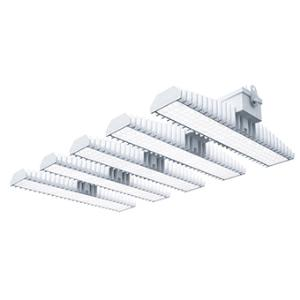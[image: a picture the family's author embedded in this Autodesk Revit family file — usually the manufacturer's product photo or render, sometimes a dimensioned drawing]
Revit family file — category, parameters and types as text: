
# Revit family: 3f_filippi_-_3f_lem_ho_ampio_3f_filippi_-_58958_a0812_-_3f_lem_5_ho_led_350_cr_ampio___vs_2ddf
name_source: partatom
category: Lighting Fixtures
units: mm (PartAtom-declared; Revit-internal decimal feet)

## family parameters
Cut with Voids When Loaded = No
Host = Face
Light Source = No
Part Type = Normal
Room Calculation Point = No
Round Connector Dimension = Use Diameter
Shared = No

## types (1)
- 3F Filippi - 3F LEM HO Ampio (1 x LED, 44256 lm, 345 W, 4000 K)
    Apparent Load = 345 VA
    Approval mark = CE
    CIE Flux Codes = 67 90 97 100 100
    Color Rendering = 80
    Color Temperature = 4000 K
    Control Gear = Electronic ballast
    Default Elevation = 1800 mm
    Description = Industrial luminaire with high light output and high luminous efficiency designed with the most innovative technologies for environments with temperature up to 55°C.

ILLUMINOTECHNICAL
Luminous efficiency 100% (DLOR 98%, ULOR 2%).
Initial luminous flux of the luminaire 44256 lm.
Direct symmetric wide distribution: the illuminated area has a rectangular shape.
Installation Interdistance Transv.D = 1.24 x hu - Long.D = 1.20 x hu.
Tabular UGR (CIE 117 - 4H-8H; S=0.25H; 70/50/20): RUG 23.8 - 23.9.
Beam angle: 82° - 83°.
Luminous efficacy 128 lm/W.
Lifetime (L93/B10): 30000 h. (tq+25°C)
Lifetime (L90/B10): 50000 h. (tq+25°C)
Lifetime (L85/B10): 80000 h. (tq+25°C)
Lifetime (L80/B10): 100000 h. (tq+25°C)
Lifetime (L85/B10): 50000 h. (tq+55°C)
Sudden decreased luminous flux after 50000 hours: 0% (C0).
Photobiological safety in compliance with IEC/TR 62778: RG0 risk exempt, (IEC 62471).
In compliance with IEC/EN 62722-2-1 - IEC/EN 62717 standards.

SOURCE
5 Mid-Power linear LED modules 70W/840.
Energy efficiency class (UE 2019/2020 - UE 2019/2015): C.
CIE 13.3 Colour rendering index: CRI >80 (R9 <50%).
IES TM-30 Fidelity Index: Rf = 84 Rg = 95.
CCT nominal colour temperature 4000 K.
Colour initial tolerance (MacAdam): SDCM 3.

MECHANICAL
Passive modular heatsinks in die-casted aluminium, painted in white colour.
To optimize the thermal management of the LED module, the heatsinks are oversized and provided with self-cleaning of cooling fins.
Wiring body in aluminium and galvanised steel anchored solidly to the sinks and thermally separated.
3F Lens lenses with high luminous efficiency, transparent methacrylate (PMMA), fixed to the LED modules.
Fixing brackets in stainless steel.
Luminaire with limited surface temperature. - D - (EN 60598-2-24)
Dimensions: 952x542 mm, height 133 mm. Weight 24.37 kg.
IP65 protection degree.
Mechanical strength to impacts IK06 (1 joule).
Glow-wire test resistance 650°C.

ELECTRICAL
Halogen Free electronic wiring 230V-50/60Hz, power factor 0.97, THD <25%, constant output current, class I, 3 driver.
Power of the luminaire 345 W.
ENEC - CE.
SAFE FLICKER: PstLM=<1 and SVM=<0.4 (IEC TR 61547-1 and IEC TR 63158), to ensure a more comfortable and safe light.
Luminaire compliant with EN 60598-2-22 for power supply from a centralised emergency system CPSS (Central Power Supply System), not incorporated in the luminaire - high risk areas excluded. The default power and flux are 100% in AC and 100% in DC.
Ambient temperature from -30°C to +55°C.
Temperature class T6 max 85°C.
Quick connection via M20 3P connector with 9-13 mm tightening range.
Power unit positioned on a separate compartment by the LED module to ensure optimum temperatures of cabling components, to be inspectable and maintainable.
Relative humidity UR: <85%.

INSTALLATION
Ceiling / Suspended / Wall.
All accessories dedicated to this product are available on the Catalog and on our website www.3F-Filippi.com.

ACCESSORIES
A0812 - Anti-glare microprismatic VS moulded glass, tempered, not flammable, with sealing gasket.
One required for each light module. The pack contains 10 pieces.

APPLICATIONS
In commercial environments, exhibition and industrial areas, stores, open areas.
Environments in which it is necessary a total protection against falling fragments (eg environments with foodstuffs or machines with moving parts or with extreme temperature changes), use luminaires with polycarbonate lenses.

WARNING
Fixture not suitable for cold stores with an ambient temperature <0°C and/or relative humidity >85%.
Luminaire designed for disposal/recycling at end-of-life.
Replaceable (LED only) light source by a professional. Replaceable control gear by a professional.
    Height = 133 mm  [stored 0.436352 ft]
    Lamp = 1 x LED
    Lamp Light Flux = 44256 lm
    Lamp Power = 345 W
    Lamp count = 1
    Length = 952 mm
    Lifetime = 50000 h
    Luminous efficacy = 128 lm/W
    Manufacturer = 3F Filippi
    ModVariant = No
    Model = 3F Filippi - 58958+A0812 - 3F LEM 5 HO LED 350 CR AMPIO + VS
    Mounting Place = Ceiling
    Mounting Type = Pendant
    Number of Poles = 1
    OnlyDefault = Yes
    Power Factor = 1
    Product Name = 3F Filippi - 3F LEM HO Ampio
    Product group = pendant luminaire
    ProductGroupID = 9
    Protection Class = Protection class I
    Protection Degree = IP 65
    RLX_Detail_Level = 1
    RLX_Emergency_Light_Flux = 0 lm
    RLX_Emergency_Type = 0
    RLX_Emergency_Type_DB = No
    RlxData = <blob elided: 129781 chars, md5=8a26e5be>
    Socket = socket
    Standby Power = 0 W
    System Light Flux = 44256 lm
    System Power = 345 W
    Type Comments = Product without accessories
    Type Image = 3f_filippi_-_lem_5__a0812.jpg
    URL = http://relux.com
    VarID = ---
    Voltage = 0 V
    Weight = 0.00 kg
    Width = 542 mm

note: [stored X ft] marks values corroborated as IEEE doubles in the binary element streams (Revit-internal decimal feet)

## geometry (parser evidence)
native form markers: Blend x4, Sweep x12
no freeform markers — native parametric forms only
